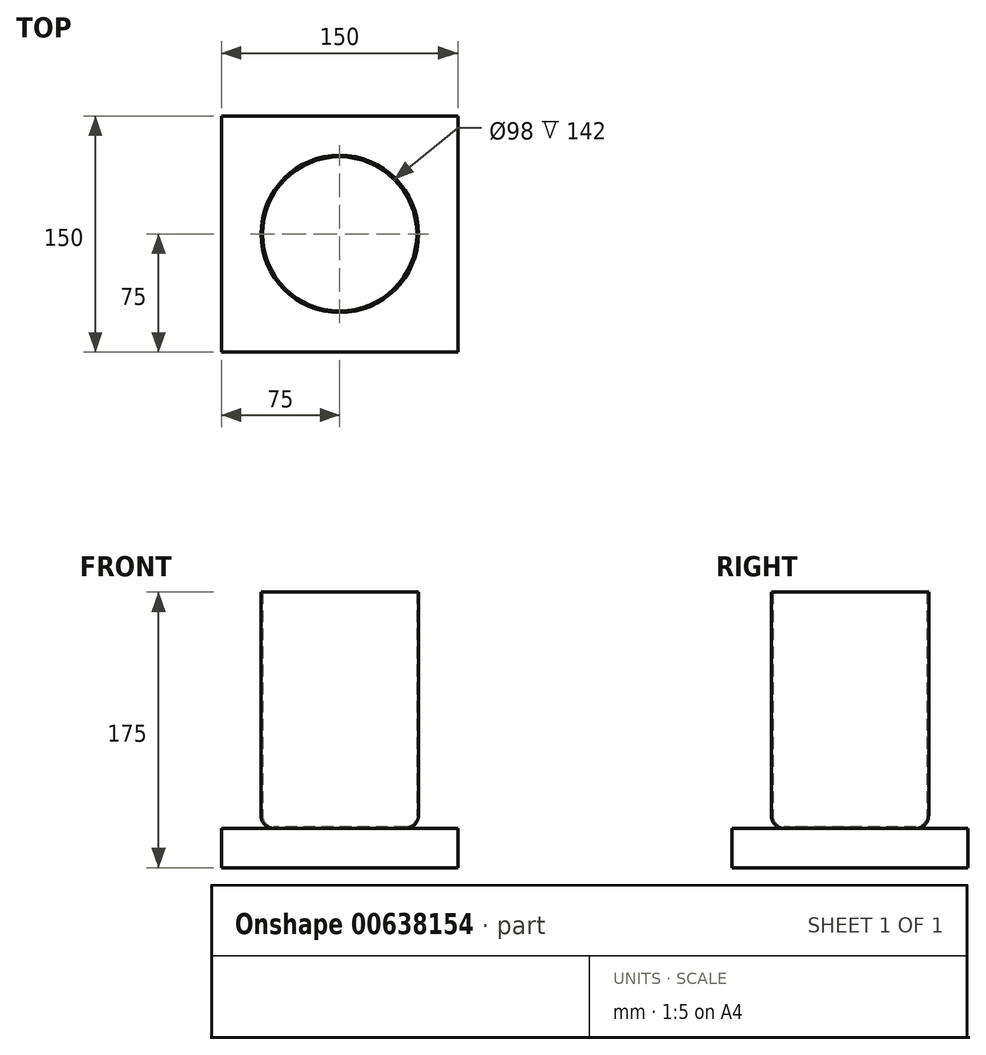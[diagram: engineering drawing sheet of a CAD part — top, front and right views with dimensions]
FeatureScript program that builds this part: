
annotation { "Feature Type Name" : "Feature", "Feature Type Description" : "" }
export const myFeature = defineFeature(function(context is Context, id is Id, definition is map)
    precondition{}
    {
        {
            var Q0;
            Q0=qCreatedBy(makeId("Top.planeOp"),FACE);
            var sketch = newSketch(context, id + "F0", { "sketchPlane" : qUnion([Q0])});
            skCircle(sketch, "E0", {"center": v(0, 0) * mm, "radius": 50 * mm});
            skSolve(sketch);
        }
        {
            var Q0;
            Q0 = qSketchRegion(id + "F0", true);
            extrude(context, id + "F1", {"entities" : qUnion([Q0]), "depth" : 150 * mm, "offsetDistance" : 25 * mm});
        }
        {
            var Q0;
            Q0=makeQuery(id+"F1.opExtrude","CAP_EDGE",EDGE,{"disambiguationData":[OSD([sQuery(id+"F0.wireOp",EDGE,"E0")])],"isStart":true});
            fillet(context, id + "F2", {"entities" : qUnion([Q0]), "radius" : 8 * mm, "tangentPropagation" : true, "allowEdgeOverflow" : false});
        }
        {
            var Q0;
            Q0=makeQuery(id+"F1.opExtrude","CAP_FACE",FACE,{"disambiguationData":[OSD([sQuery(id+"F0.wireOp",EDGE,"E0")])],"isStart":false});
            shell(context, id + "F3", {"entities" : qUnion([Q0]), "thickness" : 1 * mm});
        }
        {
            var Q0;
            Q0=qCreatedBy(makeId("Top.planeOp"),FACE);
            var sketch = newSketch(context, id + "F4", { "sketchPlane" : qUnion([Q0])});
            skLineSegment(sketch, "E1.bottom", {"start": v(-75, -75) * mm, "end": v(75, -75) * mm});
            skLineSegment(sketch, "E1.top", {"start": v(-75, 75) * mm, "end": v(75, 75) * mm});
            skLineSegment(sketch, "E1.left", {"start": v(-75, -75) * mm, "end": v(-75, 75) * mm});
            skLineSegment(sketch, "E1.right", {"start": v(75, -75) * mm, "end": v(75, 75) * mm});
            skLineSegment(sketch, "E2", {"start": v(75, 75) * mm, "end": v(-75, -75) * mm, "construction": true});
            skSolve(sketch);
        }
        {
            var Q0;
            Q0 = qSketchRegion(id + "F4", true);
            var Q1;
            Q1 = qConstructionFilter(qBodyType(qCreatedBy(id + "F4" ,EDGE), BodyType.WIRE), ConstructionObject.NO);
            extrude(context, id + "F5", {"entities" : qUnion([Q0]), "surfaceEntities" : qUnion([Q1]), "oppositeDirection" : true, "depth" : 25 * mm, "offsetDistance" : 25 * mm});
        }
    });
